# Revit family: Cumberland-Addison-Lounge1
name_source: partatom
category: Furniture
revit_build: Autodesk Revit 2014 (Build: 20130308_1515(x64)
units: mm (PartAtom-declared; Revit-internal decimal feet)

## types (3) — shared parameters
# Seat = 2
Arm Finish = CUM - Linen - Beige
Assembly Code = E2020200
Back Finish = CUM - Linen - Beige
Base Finish = CUM - Maple - Wood
Depth = 32 31/32"
Height = 31"
Keynote = 12500
Low Emitting Finish = Yes
Low Emitting Material = Yes
Manufacturer = Cumberland
Salvage or Reuse = Yes
Seat Finish = CUM - Linen - Beige
Type Comments = Addison
URL = www.cumberlandfurniture.com
zero-valued in all types: Percentage of Recycled Content

## per-type parameters (varying)
| type | Description | Seat Dist | Seat Dist 2 | Width |
| 2415 | Addison 33"W 31"H 32"D | 22 11/16" | 5 5/32" | 33" |
| 2416 | Addison 59"W 31"H 32"D | 24 11/32" | 29 1/2" | 59" |
| 2417 | Addison 83"W 31"H 32"D | 36 11/32" | 41 1/2" | 83" |

note: column(s) folded — value = type name in every type: Model

## geometry (parser evidence)
native form markers: Sweep x4
no freeform markers — native parametric forms only
